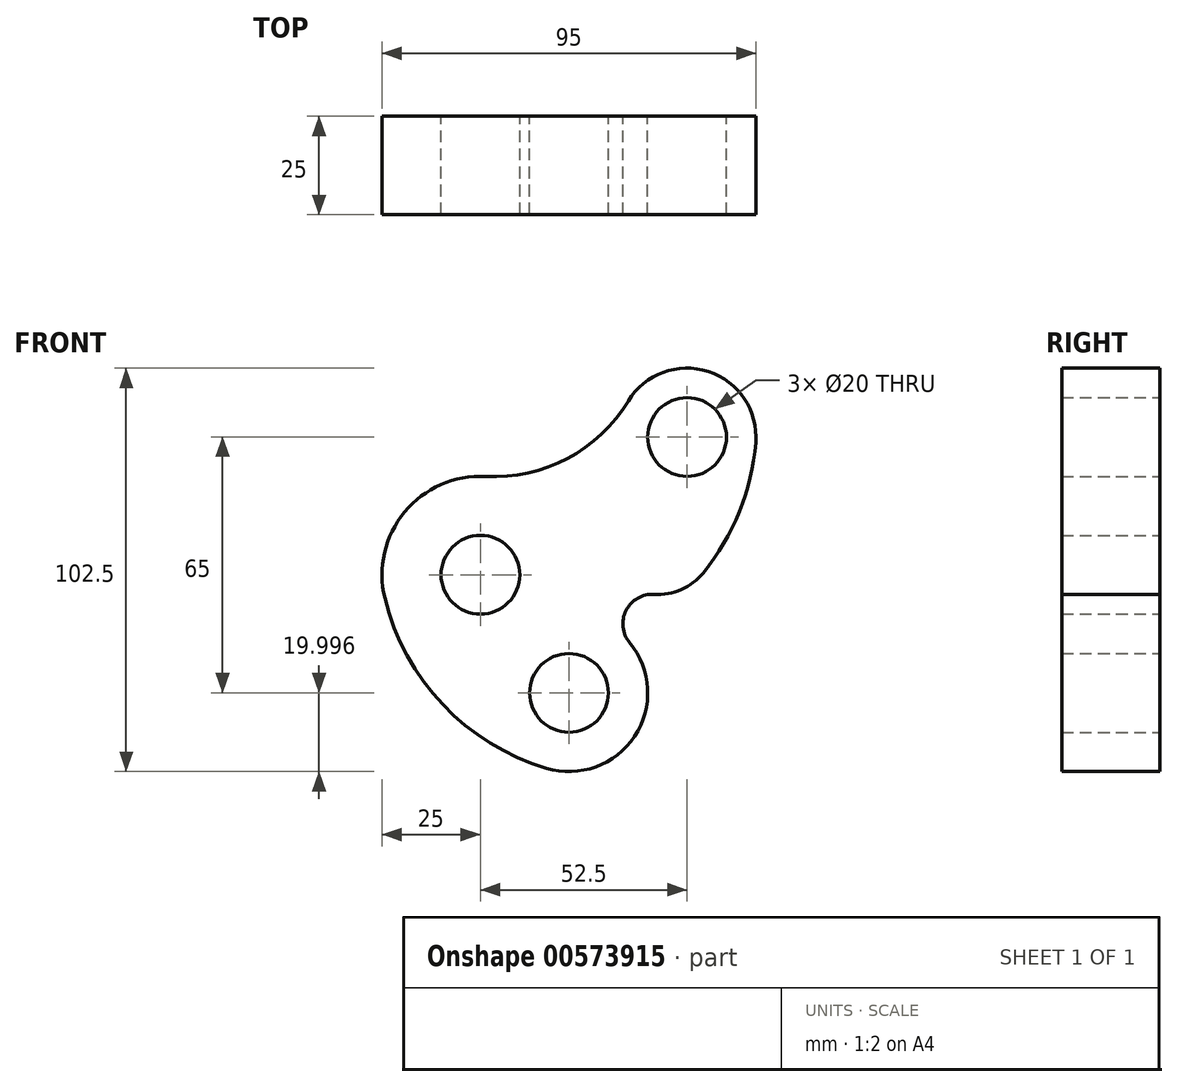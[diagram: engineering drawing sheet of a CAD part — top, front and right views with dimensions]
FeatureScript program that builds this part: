
annotation { "Feature Type Name" : "Feature", "Feature Type Description" : "" }
export const myFeature = defineFeature(function(context is Context, id is Id, definition is map)
    precondition{}
    {
        {
            var Q0;
            Q0=qCreatedBy(makeId("Front.planeOp"),FACE);
            var sketch = newSketch(context, id + "F0", { "sketchPlane" : qUnion([Q0])});
            skArc(sketch, "E0", {"start": v(13.32, 33.06) * mm, "mid": v(1.29, 51.13) * mm, "end": v(-19.07, 43.59) * mm});
            skArc(sketch, "E1", {"start": v(-39.87, -49.67) * mm, "mid": v(-17.45, -41.56) * mm, "end": v(-18.72, -17.76) * mm});
            skArc(sketch, "E2", {"start": v(-55.31, 24.45) * mm, "mid": v(-75.88, 15.43) * mm, "end": v(-80.9, -6.45) * mm});
            skArc(sketch, "E3", {"start": v(-80.9, -6.45) * mm, "mid": v(-66.13, -33.52) * mm, "end": v(-39.87, -49.67) * mm});
            skArc(sketch, "E4", {"start": v(-55.31, 24.45) * mm, "mid": v(-34.55, 29.02) * mm, "end": v(-19.07, 43.59) * mm});
            skArc(sketch, "E5", {"start": v(0, 0) * mm, "mid": v(9.17, 15.52) * mm, "end": v(13.32, 33.06) * mm});
            skArc(sketch, "E6", {"start": v(-12.5, -5.49) * mm, "mid": v(-5.59, -4.25) * mm, "end": v(0, 0) * mm});
            skArc(sketch, "E7", {"start": v(-12.5, -5.49) * mm, "mid": v(-19.63, -9.59) * mm, "end": v(-18.72, -17.76) * mm});
            skCircle(sketch, "E8", {"center": v(-4.12, 34.49) * mm, "radius": 10 * mm});
            skCircle(sketch, "E9", {"center": v(-56.62, -0.51) * mm, "radius": 10 * mm});
            skCircle(sketch, "E10", {"center": v(-34.12, -30.51) * mm, "radius": 10 * mm});
            skSolve(sketch);
        }
        {
            var Q0;
            Q0=makeQuery(id+"F0.imprint","IMPRINT",FACE,{"disambiguationData":[TD([[makeQuery(id+"F0.imprint","IMPRINT",EDGE,{"derivedFrom":sQuery(id+"F0.wireOp",EDGE,"E0")}),1.0]])]});
            extrude(context, id + "F1", {"entities" : qUnion([Q0]), "depth" : 25 * mm, "offsetDistance" : 25 * mm});
        }
    });
